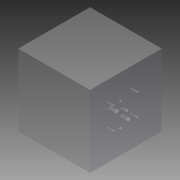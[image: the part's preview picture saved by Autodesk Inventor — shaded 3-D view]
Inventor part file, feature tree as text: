
AUTODESK INVENTOR PART (.ipt)
format: ipt  version: 2014 (Build 180170000, 170)  size: 207,872 bytes
history: native  units: mm
features: other x48, extrude x16, sketch x16
ambient origin geometry x8: Origin, YZ Plane, XZ Plane, XY Plane, X Axis, Y Axis, Z Axis, Center Point
bodies: 实体1 (feature_tree)
feature tree (80):
  extrude  "拉伸1"  Depth=101.0mm
  other  "UCS1"
  other  "UCS2"
  other  "UCS3"
  other  "UCS4"
  other  "UCS5"
  other  "UCS6"
  extrude  "拉伸2"  Depth=125.0mm
  extrude  "拉伸3"  Depth=6.8mm
  extrude  "拉伸4"  Depth=41.3mm
  extrude  "拉伸5"  TaperAngle=0.0deg  [1 undecoded]
  extrude  "拉伸6"  Depth=82.6mm
  extrude  "拉伸7"  TaperAngle=0.0deg  [1 undecoded]
  extrude  "拉伸8"  Depth=8.0mm
  extrude  "拉伸9"  Depth=16.0mm
  extrude  "拉伸10"  Depth=16.0mm
  extrude  "拉伸11"  Depth=16.0mm
  extrude  "拉伸14"  Depth=4.0mm
  extrude  "拉伸15"  Depth=4.0mm
  extrude  "拉伸16"  Depth=4.0mm
  extrude  "拉伸17"  Depth=4.0mm TaperAngle=0.0deg
  extrude  "拉伸18"  Depth=4.0mm
  sketch  "草图1"  dims[d0=250.0mm d1=0.0mm]
  sketch  "草图2"  dims[d2=0.0mm d3=0.0mm d4=0.0mm d5=0.0mm d6=0.0mm d7=0.0mm]
  sketch  "草图3"  dims[d8=0.0mm d9=0.0mm d10=0.0mm d11=0.0mm d12=0.0mm d13=0.0mm]
  sketch  "草图4"  dims[d14=0.0mm d15=0.0mm d16=0.0mm d17=0.0mm d18=0.0mm d19=0.0mm]
  sketch  "草图5"  dims[d20=0.0mm d21=0.0mm d22=0.0mm d23=0.0mm d24=0.0mm d25=0.0mm]
  sketch  "草图6"  dims[d26=0.0mm d27=0.0mm d28=0.0mm d29=0.0mm d30=0.0mm d31=0.0mm]
  sketch  "草图7"  dims[d32=0.0mm d33=0.0mm d34=0.0mm d35=0.0mm d36=0.0mm d37=0.0mm d38=101.0mm]
  sketch  "草图8"  dims[d39=95.0mm d40=125.0mm]
  sketch  "草图9"  dims[d41=124.0mm d44=6.8mm]
  sketch  "草图10"  dims[d45=38.1mm d46=41.3mm]
  sketch  "草图11"  dims[d47=76.2mm d48=0.0mm]
  sketch  "草图15"  dims[d49=76.2mm d50=82.6mm]
  sketch  "草图16"  dims[d51=82.6mm d52=0.0mm]
  sketch  "草图17"  dims[d53=26.0mm d54=0.0mm d55=8.0mm]
  sketch  "草图18"  dims[d56=16.0mm d57=0.0mm d58=16.0mm d59=-10.297443mm]
  sketch  "草图19"  dims[d60=16.0mm d61=-10.297443mm d62=16.0mm d63=-10.297443mm d64=16.0mm d65=-10.297443mm d66=14.7mm d67=54.0mm d68=11.1mm d69=31.0mm d70=0.0mm d71=31.0mm d72=-10.297443mm d73=14.7mm d74=52.4mm d75=9.5mm d76=30.0mm d77=0.0mm d78=30.0mm d79=-10.297443mm d87=11.1mm d88=46.8mm d89=38.0mm d90=22.2mm d91=0.0mm d92=22.2mm d93=-10.297443mm d94=10.4mm d95=23.8mm d96=3.2mm d97=79.4mm d98=23.8mm d99=4.0mm d100=0.0mm d101=4.0mm d102=-10.297443mm d103=4.0mm d104=-8.552113mm]
  other  "UCS1: YZ 平面"
  other  "UCS1: XZ 平面"
  other  "UCS1: XY 平面"
  other  "UCS1: X 轴"
  other  "UCS1: Y 轴"
  other  "UCS1: Z 轴"
  other  "UCS1: 原点"
  other  "UCS2: YZ 平面"
  other  "UCS2: XZ 平面"
  other  "UCS2: XY 平面"
  other  "UCS2: X 轴"
  other  "UCS2: Y 轴"
  other  "UCS2: Z 轴"
  other  "UCS2: 原点"
  other  "UCS3: YZ 平面"
  other  "UCS3: XZ 平面"
  other  "UCS3: XY 平面"
  other  "UCS3: X 轴"
  other  "UCS3: Y 轴"
  other  "UCS3: Z 轴"
  other  "UCS3: 原点"
  other  "UCS4: YZ 平面"
  other  "UCS4: XZ 平面"
  other  "UCS4: XY 平面"
  other  "UCS4: X 轴"
  other  "UCS4: Y 轴"
  other  "UCS4: Z 轴"
  other  "UCS4: 原点"
  other  "UCS5: YZ 平面"
  other  "UCS5: XZ 平面"
  other  "UCS5: XY 平面"
  other  "UCS5: X 轴"
  other  "UCS5: Y 轴"
  other  "UCS5: Z 轴"
  other  "UCS5: 原点"
  other  "UCS6: YZ 平面"
  other  "UCS6: XZ 平面"
  other  "UCS6: XY 平面"
  other  "UCS6: X 轴"
  other  "UCS6: Y 轴"
  other  "UCS6: Z 轴"
  other  "UCS6: 原点"
note: 2 required parameter values undecoded (feature->parameter linkage not recoverable at this tier; creation-order binding heuristic only, values carry confidence <= 0.55)
